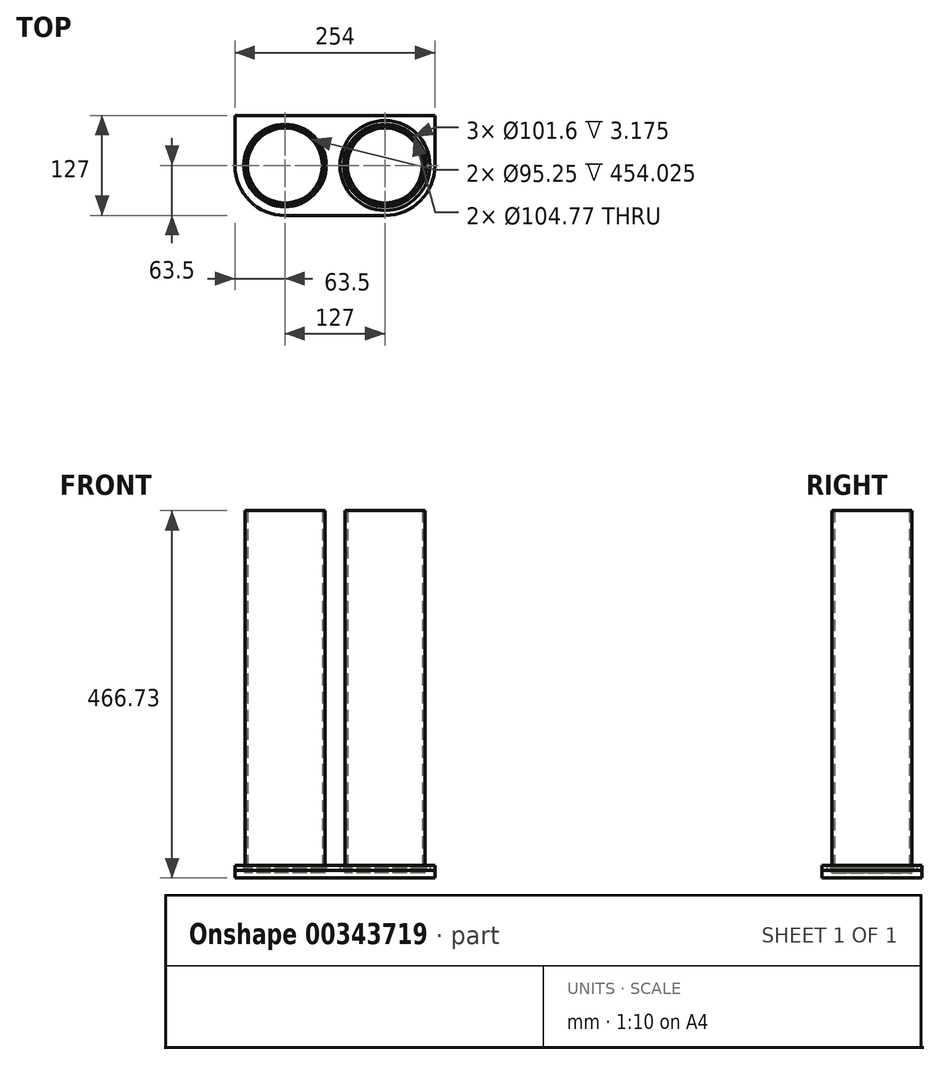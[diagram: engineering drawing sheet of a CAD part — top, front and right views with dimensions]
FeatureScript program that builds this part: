
annotation { "Feature Type Name" : "Feature", "Feature Type Description" : "" }
export const myFeature = defineFeature(function(context is Context, id is Id, definition is map)
    precondition{}
    {
        {
            var Q0;
            Q0=qCreatedBy(makeId("Top.planeOp"),FACE);
            var sketch = newSketch(context, id + "F0", { "sketchPlane" : qUnion([Q0])});
            skCircle(sketch, "E0", {"center": v(0, 0) * mm, "radius": 57.15 * mm});
            skSolve(sketch);
        }
        {
            var Q0;
            Q0=makeQuery(id+"F0.imprint","IMPRINT",FACE,{"disambiguationData":[TD([[makeQuery(id+"F0.imprint","IMPRINT",EDGE,{"derivedFrom":sQuery(id+"F0.wireOp",EDGE,"E0")}),1.0]])]});
            extrude(context, id + "F1", {"entities" : qUnion([Q0]), "depth" : 6.35 * mm});
        }
        {
            var Q0;
            Q0=qSketchRegion(id+"FBIn8MUJCKqfJnR_2",true);
            var Q1;
            Q1=makeQuery(id+"F1.opExtrude","CAP_FACE",FACE,{"disambiguationData":[OSD([sQuery(id+"F0.wireOp",EDGE,"E0"),sQuery(id+"F0.wireOp",EDGE,"d5b0e4c8-623b-4571-8e95-f6619596fdad")])],"isStart":false});
            extrude(context, id + "F2", {"entities" : qUnion([Q0, Q1]), "operationType" : NewBodyOperationType.REMOVE, "depth" : 25.4 * mm});
        }
        {
            var Q0;
            Q0=qCreatedBy(makeId("Top.planeOp"),FACE);
            var sketch = newSketch(context, id + "F3", { "sketchPlane" : qUnion([Q0])});
            skLineSegment(sketch, "E1", {"start": v(-190.5, 0) * mm, "end": v(63.5, 0) * mm, "construction": true});
            skCircle(sketch, "E2", {"center": v(0, 0) * mm, "radius": 50.8 * mm, "construction": true});
            skArc(sketch, "E3", {"start": v(-190.5, 0) * mm, "mid": v(-171.9, -44.9) * mm, "end": v(-127, -63.5) * mm});
            skArc(sketch, "E4.trimOffspring", {"start": v(0, -63.5) * mm, "mid": v(44.9, -44.9) * mm, "end": v(63.5, 0) * mm});
            skPoint(sketch, "E5.visualSharp", {"position": v(-63.5, 0) * mm});
            skLineSegment(sketch, "E6", {"start": v(-127, -63.5) * mm, "end": v(0, -63.5) * mm});
            skLineSegment(sketch, "E7", {"start": v(-190.5, 63.5) * mm, "end": v(63.5, 63.5) * mm});
            skLineSegment(sketch, "E8", {"start": v(63.5, 0) * mm, "end": v(63.5, 63.5) * mm});
            skLineSegment(sketch, "E9", {"start": v(-190.5, 0) * mm, "end": v(-190.5, 63.5) * mm});
            skPoint(sketch, "E9.endSnap0", {"position": v(-190.5, 0) * mm});
            skSolve(sketch);
        }
        {
            var Q0;
            Q0=qSketchRegion(id+"F3",true);
            extrude(context, id + "F4", {"entities" : qUnion([Q0]), "oppositeDirection" : true, "depth" : 9.52 * mm});
        }
        {
            var Q0;
            Q0=qCreatedBy(makeId("Top.planeOp"),FACE);
            var sketch = newSketch(context, id + "F5", { "sketchPlane" : qUnion([Q0])});
            skCircle(sketch, "E10", {"center": v(0, 0) * mm, "radius": 50.8 * mm});
            skCircle(sketch, "E11", {"center": v(0, 0) * mm, "radius": 47.63 * mm});
            skCircle(sketch, "E12", {"center": v(-127, 0) * mm, "radius": 50.8 * mm});
            skCircle(sketch, "E13", {"center": v(-127, 0) * mm, "radius": 47.63 * mm});
            skLineSegment(sketch, "E14", {"start": v(0, 0) * mm, "end": v(-127, 0) * mm, "construction": true});
            skSolve(sketch);
        }
        {
            var Q0;
            Q0=qSketchRegion(id+"F5",true);
            extrude(context, id + "F6", {"entities" : qUnion([Q0]), "depth" : 457.2 * mm});
        }
        {
            var Q0;
            Q0 = qSketchRegion(id + "F5", true);
            extrude(context, id + "F7", {"entities" : qUnion([Q0]), "operationType" : NewBodyOperationType.REMOVE, "depth" : 3.17 * mm});
        }
        {
            var Q0;
            Q0 = qSketchRegion(id + "F5", true);
            extrude(context, id + "F8", {"entities" : qUnion([Q0]), "operationType" : NewBodyOperationType.REMOVE, "oppositeDirection" : true, "depth" : 3.17 * mm});
        }
        {
            var Q0;
            Q0=makeQuery(id+"F3.imprint","IMPRINT",FACE,{"disambiguationData":[TD([[makeQuery(id+"F3.imprint","IMPRINT",EDGE,{"derivedFrom":sQuery(id+"F3.wireOp",EDGE,"E3")}),1.0]])]});
            extrude(context, id + "F9", {"entities" : qUnion([Q0]), "depth" : 6.35 * mm});
        }
        {
            var Q0;
            Q0=sQuery(id+"F5.wireOp",VERTEX,"E13.center");
            var Q1;
            Q1=sQuery(id+"F5.wireOp",VERTEX,"E11.center");
            var Q2;
            Q2=makeQuery(id+"F9.opExtrude","SWEPT_BODY",BODY,{"disambiguationData":[OSD([sQuery(id+"F3.wireOp",EDGE,"E3"),sQuery(id+"F3.wireOp",EDGE,"E4.trimOffspring"),sQuery(id+"F3.wireOp",EDGE,"E6"),sQuery(id+"F3.wireOp",EDGE,"E7"),sQuery(id+"F3.wireOp",EDGE,"E8"),sQuery(id+"F3.wireOp",EDGE,"E9")])]});
            hole(context, id + "F10", {"style" : HoleStyle.SIMPLE, "endStyle" : HoleEndStyle.THROUGH, "oppositeDirection" : true, "holeDiameter" : 104.77 * mm, "isTappedThrough" : true, "tappedDepth" : 12.7 * mm, "tapClearance" : 3, "locations" : qUnion([Q0, Q1]), "scope" : qUnion([Q2])});
        }
    });
